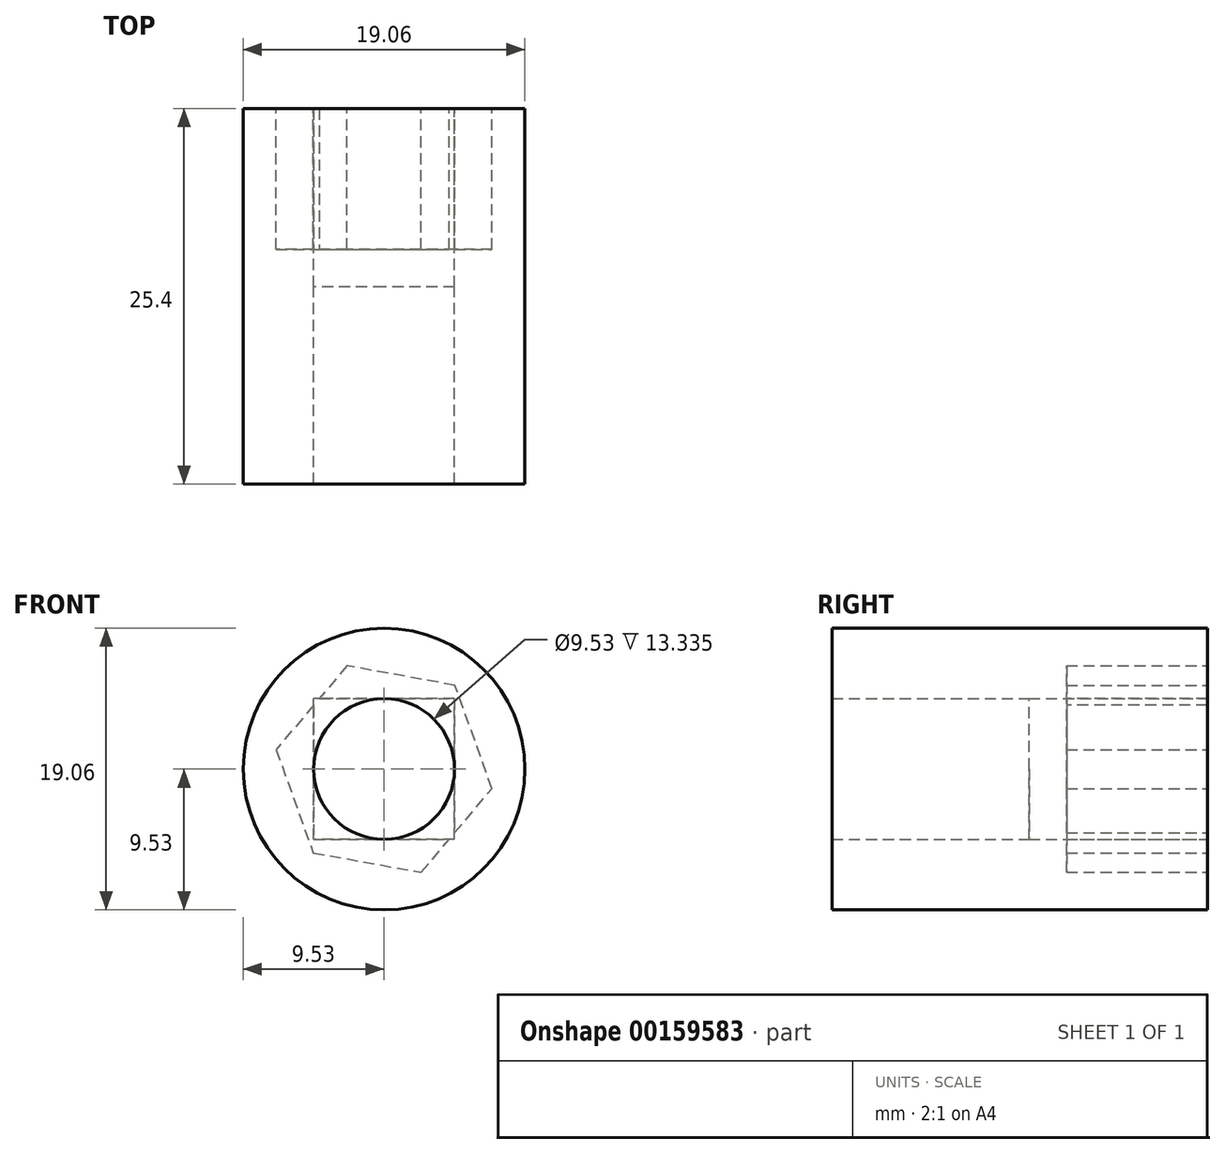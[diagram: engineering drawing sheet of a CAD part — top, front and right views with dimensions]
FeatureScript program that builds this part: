
annotation { "Feature Type Name" : "Feature", "Feature Type Description" : "" }
export const myFeature = defineFeature(function(context is Context, id is Id, definition is map)
    precondition{}
    {
        {
            var Q0;
            Q0=qCreatedBy(makeId("Front.planeOp"),FACE);
            var sketch = newSketch(context, id + "F0", { "sketchPlane" : qUnion([Q0])});
            skCircle(sketch, "E0", {"center": v(0, 0) * mm, "radius": 9.53 * mm});
            skSolve(sketch);
        }
        {
            var Q0;
            Q0 = qSketchRegion(id + "F0", true);
            extrude(context, id + "F1", {"entities" : qUnion([Q0]), "depth" : 25.4 * mm});
        }
        {
            var Q0;
            Q0=qCreatedBy(makeId("Front.planeOp"),FACE);
            var sketch = newSketch(context, id + "F2", { "sketchPlane" : qUnion([Q0])});
            skLineSegment(sketch, "E1.bottom", {"start": v(4.76, -4.76) * mm, "end": v(-4.76, -4.76) * mm});
            skLineSegment(sketch, "E1.top", {"start": v(4.76, 4.76) * mm, "end": v(-4.76, 4.76) * mm});
            skLineSegment(sketch, "E1.left", {"start": v(4.76, -4.76) * mm, "end": v(4.76, 4.76) * mm});
            skLineSegment(sketch, "E1.right", {"start": v(-4.76, -4.76) * mm, "end": v(-4.76, 4.76) * mm});
            skPoint(sketch, "E1.middle", {"position": v(0, 0) * mm});
            skCircle(sketch, "E2", {"center": v(0, 0) * mm, "radius": 4.76 * mm});
            skSolve(sketch);
        }
        {
            var Q0;
            {var subQ0=sQuery(id+"F2.wireOp",EDGE,"E2");var subQ1=makeQuery(id+"F2.imprint","INTERSECT",VERTEX,{"derivedFrom":[sQuery(id+"F2.wireOp",EDGE,"E1.top"),subQ0]});Q0=makeQuery(id+"F2.imprint","IMPRINT",FACE,{"disambiguationData":[TD([[makeQuery(id+"F2.imprint","IMPRINT",EDGE,{"disambiguationData":[TD([[subQ1,1.0]])],"derivedFrom":subQ0}),1.0]])]});}
            extrude(context, id + "F3", {"entities" : qUnion([Q0]), "operationType" : NewBodyOperationType.REMOVE, "endBound" : BoundingType.THROUGH_ALL, "depth" : 25.4 * mm});
        }
        {
            var Q0;
            Q0 = qSketchRegion(id + "F2", true);
            extrude(context, id + "F4", {"entities" : qUnion([Q0]), "operationType" : NewBodyOperationType.REMOVE, "depth" : 12.06 * mm});
        }
        {
            var Q0;
            Q0=makeQuery(id+"F1.opExtrude","CAP_FACE",FACE,{"disambiguationData":[OSD([sQuery(id+"F0.wireOp",EDGE,"E0")])],"isStart":true});
            var sketch = newSketch(context, id + "F5", { "sketchPlane" : qUnion([Q0])});
            skCircle(sketch, "E3.cCircle", {"center": v(0, 0) * mm, "radius": 6.43 * mm, "construction": true});
            skLineSegment(sketch, "E3.0", {"start": v(7.3, 1.32) * mm, "end": v(4.8, -5.66) * mm});
            skLineSegment(sketch, "E3.1", {"start": v(4.8, -5.66) * mm, "end": v(-2.5, -6.98) * mm});
            skLineSegment(sketch, "E3.2", {"start": v(-2.5, -6.98) * mm, "end": v(-7.3, -1.32) * mm});
            skLineSegment(sketch, "E3.3", {"start": v(-7.3, -1.32) * mm, "end": v(-4.8, 5.66) * mm});
            skLineSegment(sketch, "E3.4", {"start": v(-4.8, 5.66) * mm, "end": v(2.5, 6.98) * mm});
            skLineSegment(sketch, "E3.5", {"start": v(2.5, 6.98) * mm, "end": v(7.3, 1.32) * mm});
            skPoint(sketch, "E3.0.midPoint", {"position": v(6.05, -2.17) * mm});
            skSolve(sketch);
        }
        {
            var Q0;
            Q0 = qSketchRegion(id + "F5", true);
            extrude(context, id + "F6", {"entities" : qUnion([Q0]), "operationType" : NewBodyOperationType.REMOVE, "oppositeDirection" : true, "depth" : 9.52 * mm});
        }
    });
